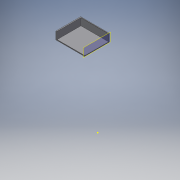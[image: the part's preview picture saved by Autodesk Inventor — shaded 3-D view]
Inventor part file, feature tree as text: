
AUTODESK INVENTOR PART (.ipt)
format: ipt  version: 2016 SP2 (Build 200236200, 236)  size: 110,592 bytes
history: native  units: mm
features: reference x7, sketch x3, extrude x2, plane x1
ambient origin geometry x8: Origin, YZ Plane, XZ Plane, XY Plane, X Axis, Y Axis, Z Axis, Center Point
bodies: Volumenkörper1 (feature_tree)
feature tree (13):
  plane  "Arbeitsebene1"
  extrude  "Extrusion1"  Depth=92.5mm TaperAngle=0.0deg
  sketch  "Skizze2"  dims[d3=3.0mm d4=0.0mm]
  extrude  "Extrusion2"  [1 undecoded]
  sketch  "Skizze1"  dims[d0=2.0mm d1=92.5mm d2=0.0mm]
  reference  "Referenz1"
  reference  "Referenz2"
  reference  "Referenz3"
  reference  "Referenz4"
  reference  "Referenz5"
  reference  "Referenz6"
  reference  "Referenz7"
  sketch  "Skizze3"
note: 1 required parameter value undecoded (feature->parameter linkage not recoverable at this tier; creation-order binding heuristic only, values carry confidence <= 0.55)
